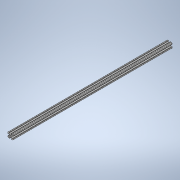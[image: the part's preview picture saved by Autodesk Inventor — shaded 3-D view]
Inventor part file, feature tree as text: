
AUTODESK INVENTOR PART (.ipt)
format: ipt  version: 2020 (Build 240168000, 168)  size: 241,664 bytes
history: native  units: in
note: dims shown in document units (in); Inventor stores cm internally (conversion verified against a paired STEP export)
features: extrude x1, sketch x1
ambient origin geometry x8: Origin, YZ Plane, XZ Plane, XY Plane, X Axis, Y Axis, Z Axis, Center Point
bodies: Solid1 (feature_tree)
feature tree (2):
  extrude  "Extrusion1"  [1 undecoded]
  sketch  "Sketch1"  dims[d0=31.0in d1=0.0in]
note: 1 required parameter value undecoded (feature->parameter linkage not recoverable at this tier; creation-order binding heuristic only, values carry confidence <= 0.55)
